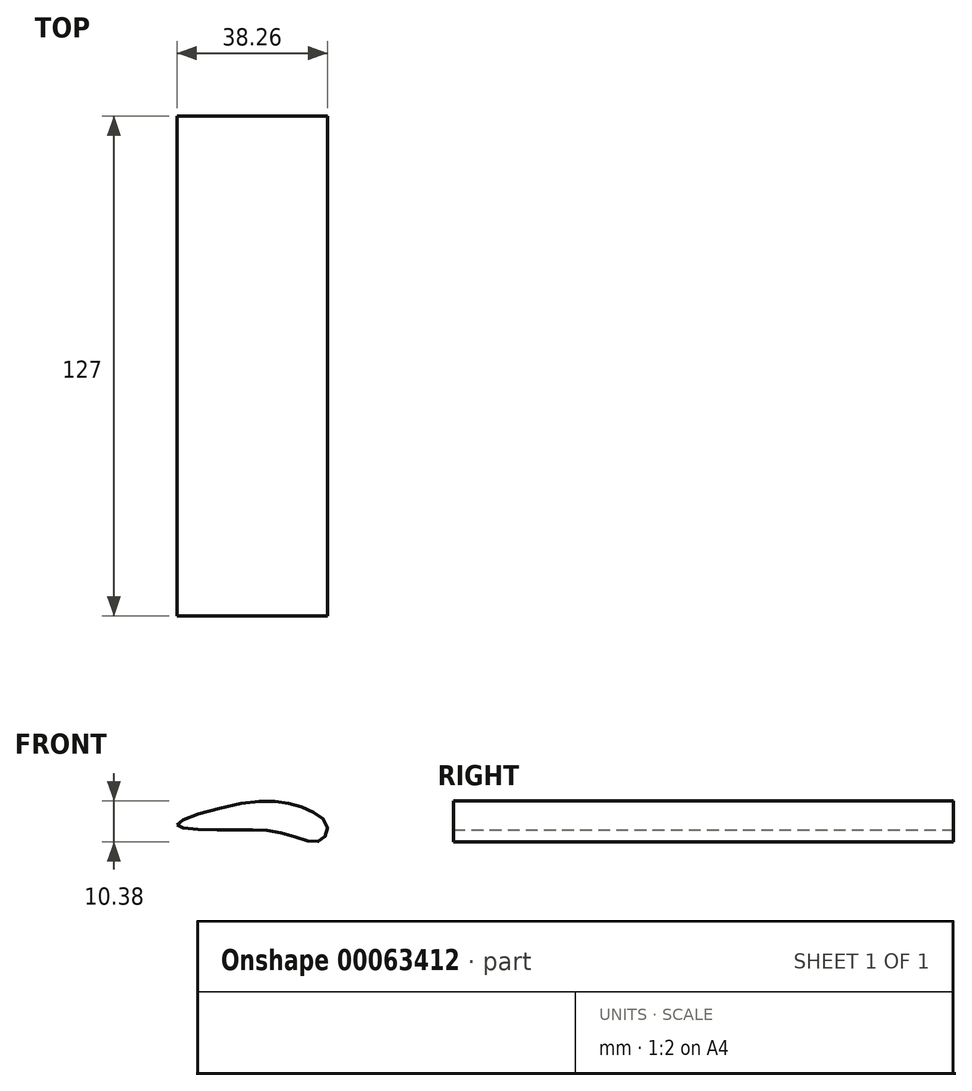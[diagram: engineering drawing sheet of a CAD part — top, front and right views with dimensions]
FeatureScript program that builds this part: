
annotation { "Feature Type Name" : "Feature", "Feature Type Description" : "" }
export const myFeature = defineFeature(function(context is Context, id is Id, definition is map)
    precondition{}
    {
        {
            var Q0;
            Q0=qCreatedBy(makeId("Front.planeOp"),FACE);
            var sketch = newSketch(context, id + "F0", { "sketchPlane" : qUnion([Q0])});
            skFitSpline(sketch, "E0", {"points": [v(0, 0) * mm, v(17.06, 5.55) * mm, v(31.14, 4.72) * mm, v(38.1, 0) * mm, v(36.44, -4.06) * mm, v(27.5, -2.24) * mm, v(12.76, -1.24) * mm, v(0, 0) * mm]});
            skSolve(sketch);
        }
        {
            var Q0;
            Q0=qSketchRegion(id+"F0",true);
            extrude(context, id + "F1", {"entities" : qUnion([Q0]), "depth" : 127 * mm});
        }
    });
